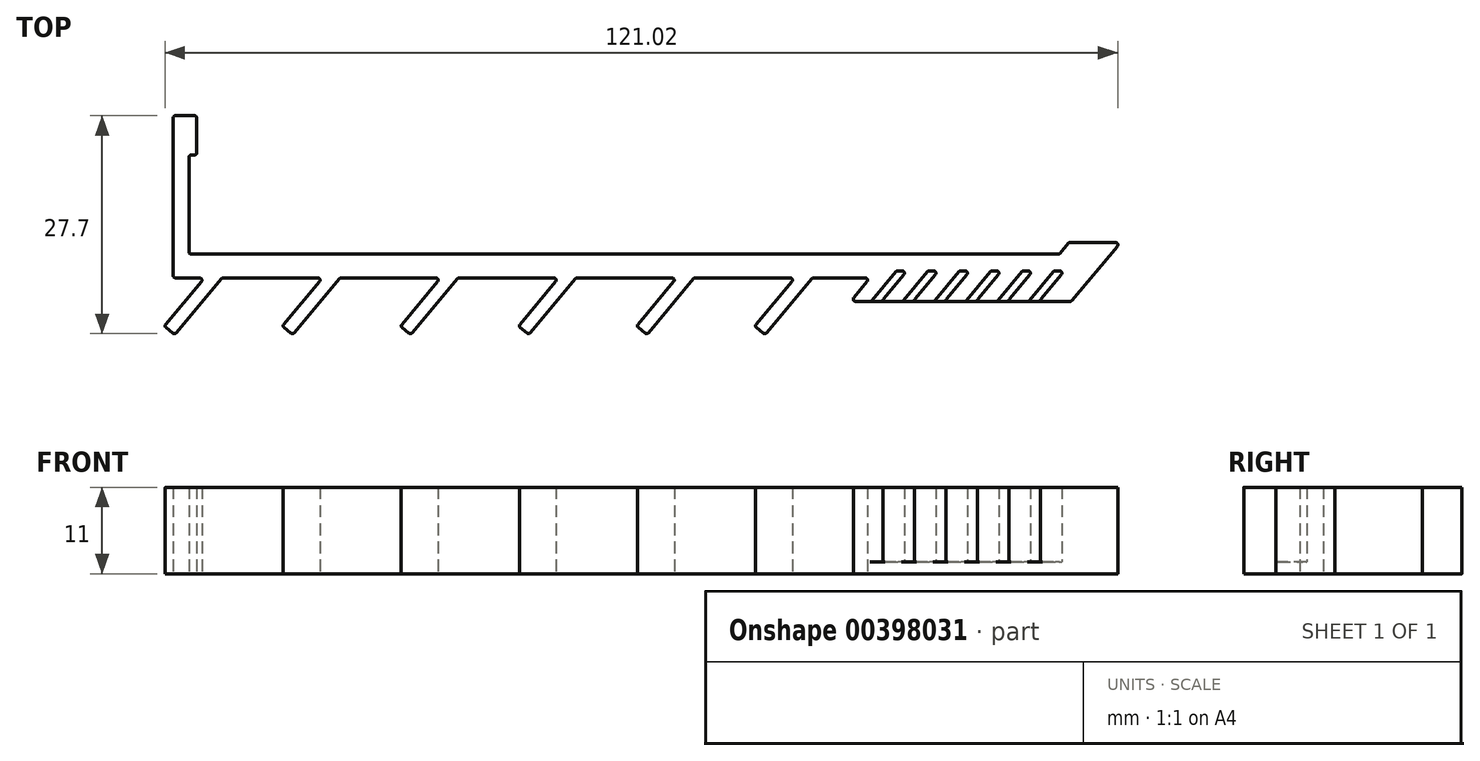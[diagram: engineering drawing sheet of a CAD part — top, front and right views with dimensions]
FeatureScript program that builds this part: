
annotation { "Feature Type Name" : "Feature", "Feature Type Description" : "" }
export const myFeature = defineFeature(function(context is Context, id is Id, definition is map)
    precondition{}
    {
        {
            var Q0;
            Q0=qCreatedBy(makeId("Top.planeOp"),FACE);
            var sketch = newSketch(context, id + "F0", { "sketchPlane" : qUnion([Q0])});
            skLineSegment(sketch, "E0", {"start": v(-67.4, 20.3) * mm, "end": v(-67.4, 0.3) * mm});
            skLineSegment(sketch, "E1", {"start": v(45.02, 3) * mm, "end": v(-65.1, 3) * mm});
            skLineSegment(sketch, "E2", {"start": v(-64.7, 20.6) * mm, "end": v(-67.1, 20.6) * mm});
            skLineSegment(sketch, "E3", {"start": v(-65.4, 3.3) * mm, "end": v(-65.4, 15.3) * mm});
            skLineSegment(sketch, "E4", {"start": v(-65.1, 15.6) * mm, "end": v(-64.7, 15.6) * mm});
            skLineSegment(sketch, "E5.trimOffspring", {"start": v(-64.4, 15.9) * mm, "end": v(-64.4, 20.3) * mm});
            skPoint(sketch, "E6.visualSharp", {"position": v(-64.4, 15.6) * mm});
            skArc(sketch, "E6.filletArc", {"start": v(-64.7, 15.6) * mm, "mid": v(-64.49, 15.69) * mm, "end": v(-64.4, 15.9) * mm});
            skPoint(sketch, "E7.visualSharp", {"position": v(-65.4, 15.6) * mm});
            skArc(sketch, "E7.filletArc", {"start": v(-65.1, 15.6) * mm, "mid": v(-65.31, 15.51) * mm, "end": v(-65.4, 15.3) * mm});
            skPoint(sketch, "E8.visualSharp", {"position": v(-64.4, 20.6) * mm});
            skArc(sketch, "E8.filletArc", {"start": v(-64.4, 20.3) * mm, "mid": v(-64.49, 20.51) * mm, "end": v(-64.7, 20.6) * mm});
            skPoint(sketch, "E9.visualSharp", {"position": v(-67.4, 20.6) * mm});
            skArc(sketch, "E9.filletArc", {"start": v(-67.1, 20.6) * mm, "mid": v(-67.31, 20.51) * mm, "end": v(-67.4, 20.3) * mm});
            skPoint(sketch, "E10.visualSharp", {"position": v(-67.4, 0) * mm});
            skArc(sketch, "E10.filletArc", {"start": v(-67.4, 0.3) * mm, "mid": v(-67.31, 0.09) * mm, "end": v(-67.1, 0) * mm});
            skLineSegment(sketch, "E11", {"start": v(-63.81, -0.5) * mm, "end": v(-68.35, -5.9) * mm});
            skLineSegment(sketch, "E12", {"start": v(-68.31, -6.32) * mm, "end": v(-67.47, -7.03) * mm});
            skLineSegment(sketch, "E13", {"start": v(-67.05, -7) * mm, "end": v(-61.27, -0.1) * mm});
            skLineSegment(sketch, "E14.1.0.0", {"start": v(-53.31, -6.32) * mm, "end": v(-52.47, -7.03) * mm});
            skLineSegment(sketch, "E14.1.0.1", {"start": v(-52.05, -7) * mm, "end": v(-46.27, -0.1) * mm});
            skLineSegment(sketch, "E14.1.0.2", {"start": v(-48.81, -0.5) * mm, "end": v(-53.35, -5.9) * mm});
            skLineSegment(sketch, "E14.2.0.0", {"start": v(-38.31, -6.32) * mm, "end": v(-37.47, -7.03) * mm});
            skLineSegment(sketch, "E14.2.0.1", {"start": v(-37.05, -7) * mm, "end": v(-31.27, -0.1) * mm});
            skLineSegment(sketch, "E14.2.0.2", {"start": v(-33.81, -0.5) * mm, "end": v(-38.35, -5.9) * mm});
            skLineSegment(sketch, "E14.3.0.0", {"start": v(-23.31, -6.32) * mm, "end": v(-22.47, -7.03) * mm});
            skLineSegment(sketch, "E14.3.0.1", {"start": v(-22.05, -7) * mm, "end": v(-16.27, -0.1) * mm});
            skLineSegment(sketch, "E14.3.0.2", {"start": v(-18.81, -0.5) * mm, "end": v(-23.35, -5.9) * mm});
            skLineSegment(sketch, "E14.4.0.0", {"start": v(-8.31, -6.32) * mm, "end": v(-7.47, -7.03) * mm});
            skLineSegment(sketch, "E14.4.0.1", {"start": v(-7.05, -7) * mm, "end": v(-1.27, -0.1) * mm});
            skLineSegment(sketch, "E14.4.0.2", {"start": v(-3.81, -0.5) * mm, "end": v(-8.35, -5.9) * mm});
            skLineSegment(sketch, "E14.5.0.0", {"start": v(6.69, -6.32) * mm, "end": v(7.53, -7.03) * mm});
            skLineSegment(sketch, "E14.5.0.1", {"start": v(7.95, -7) * mm, "end": v(13.73, -0.1) * mm});
            skLineSegment(sketch, "E14.5.0.2", {"start": v(11.19, -0.5) * mm, "end": v(6.65, -5.9) * mm});
            skLineSegment(sketch, "E14.direction1", {"start": v(-68.54, -6.13) * mm, "end": v(-53.54, -6.13) * mm, "construction": true});
            skLineSegment(sketch, "E15.top", {"start": v(19.3, -3) * mm, "end": v(21.12, -3) * mm});
            skLineSegment(sketch, "E15.left", {"start": v(20.75, -0.5) * mm, "end": v(19.06, -2.5) * mm});
            skLineSegment(sketch, "E16", {"start": v(20.52, 0) * mm, "end": v(13.96, 0) * mm});
            skLineSegment(sketch, "E17", {"start": v(10.96, 0) * mm, "end": v(-1.04, 0) * mm});
            skLineSegment(sketch, "E18", {"start": v(-4.04, 0) * mm, "end": v(-16.04, 0) * mm});
            skLineSegment(sketch, "E19", {"start": v(-19.04, 0) * mm, "end": v(-31.04, 0) * mm});
            skLineSegment(sketch, "E20", {"start": v(-34.04, 0) * mm, "end": v(-46.04, 0) * mm});
            skLineSegment(sketch, "E21", {"start": v(-49.04, 0) * mm, "end": v(-61.04, 0) * mm});
            skLineSegment(sketch, "E22", {"start": v(-64.04, 0) * mm, "end": v(-67.1, 0) * mm});
            skLineSegment(sketch, "E23", {"start": v(52.53, 4) * mm, "end": v(46.74, -2.9) * mm});
            skPoint(sketch, "E24.visualSharp", {"position": v(46.65, -3) * mm});
            skArc(sketch, "E24.filletArc", {"start": v(46.51, -3) * mm, "mid": v(46.64, -2.97) * mm, "end": v(46.74, -2.9) * mm});
            skPoint(sketch, "E25.visualSharp", {"position": v(18.65, -3) * mm});
            skArc(sketch, "E25.filletArc", {"start": v(19.06, -2.5) * mm, "mid": v(19.02, -2.83) * mm, "end": v(19.3, -3) * mm});
            skArc(sketch, "E26.filletArc", {"start": v(20.75, -0.5) * mm, "mid": v(20.8, -0.17) * mm, "end": v(20.52, 0) * mm});
            skPoint(sketch, "E27.visualSharp", {"position": v(-61.18, 0) * mm});
            skArc(sketch, "E27.filletArc", {"start": v(-61.04, 0) * mm, "mid": v(-61.17, -0.03) * mm, "end": v(-61.27, -0.1) * mm});
            skPoint(sketch, "E28.visualSharp", {"position": v(-63.4, 0) * mm});
            skArc(sketch, "E28.filletArc", {"start": v(-63.81, -0.5) * mm, "mid": v(-63.77, -0.17) * mm, "end": v(-64.04, 0) * mm});
            skPoint(sketch, "E29.visualSharp", {"position": v(-48.4, 0) * mm});
            skArc(sketch, "E29.filletArc", {"start": v(-48.81, -0.5) * mm, "mid": v(-48.77, -0.17) * mm, "end": v(-49.04, 0) * mm});
            skPoint(sketch, "E30.visualSharp", {"position": v(-46.18, 0) * mm});
            skArc(sketch, "E30.filletArc", {"start": v(-46.04, 0) * mm, "mid": v(-46.17, -0.03) * mm, "end": v(-46.27, -0.1) * mm});
            skPoint(sketch, "E31.visualSharp", {"position": v(-33.4, 0) * mm});
            skArc(sketch, "E31.filletArc", {"start": v(-33.81, -0.5) * mm, "mid": v(-33.77, -0.17) * mm, "end": v(-34.04, 0) * mm});
            skPoint(sketch, "E32.visualSharp", {"position": v(-31.18, 0) * mm});
            skArc(sketch, "E32.filletArc", {"start": v(-31.04, 0) * mm, "mid": v(-31.17, -0.03) * mm, "end": v(-31.27, -0.1) * mm});
            skPoint(sketch, "E33.visualSharp", {"position": v(-18.4, 0) * mm});
            skArc(sketch, "E33.filletArc", {"start": v(-18.81, -0.5) * mm, "mid": v(-18.77, -0.17) * mm, "end": v(-19.04, 0) * mm});
            skPoint(sketch, "E34.visualSharp", {"position": v(-16.18, 0) * mm});
            skArc(sketch, "E34.filletArc", {"start": v(-16.04, 0) * mm, "mid": v(-16.17, -0.03) * mm, "end": v(-16.27, -0.1) * mm});
            skPoint(sketch, "E35.visualSharp", {"position": v(-3.4, 0) * mm});
            skArc(sketch, "E35.filletArc", {"start": v(-3.81, -0.5) * mm, "mid": v(-3.77, -0.17) * mm, "end": v(-4.04, 0) * mm});
            skPoint(sketch, "E36.visualSharp", {"position": v(-1.18, 0) * mm});
            skArc(sketch, "E36.filletArc", {"start": v(-1.04, 0) * mm, "mid": v(-1.17, -0.03) * mm, "end": v(-1.27, -0.1) * mm});
            skPoint(sketch, "E37.visualSharp", {"position": v(11.6, 0) * mm});
            skArc(sketch, "E37.filletArc", {"start": v(11.19, -0.5) * mm, "mid": v(11.23, -0.17) * mm, "end": v(10.96, 0) * mm});
            skPoint(sketch, "E38.visualSharp", {"position": v(13.82, 0) * mm});
            skArc(sketch, "E38.filletArc", {"start": v(13.96, 0) * mm, "mid": v(13.83, -0.03) * mm, "end": v(13.73, -0.1) * mm});
            skPoint(sketch, "E39.visualSharp", {"position": v(7.76, -7.22) * mm});
            skArc(sketch, "E39.filletArc", {"start": v(7.53, -7.03) * mm, "mid": v(7.75, -7.1) * mm, "end": v(7.95, -7) * mm});
            skPoint(sketch, "E40.visualSharp", {"position": v(6.46, -6.13) * mm});
            skArc(sketch, "E40.filletArc", {"start": v(6.65, -5.9) * mm, "mid": v(6.58, -6.12) * mm, "end": v(6.69, -6.32) * mm});
            skPoint(sketch, "E41.visualSharp", {"position": v(-7.24, -7.22) * mm});
            skArc(sketch, "E41.filletArc", {"start": v(-7.47, -7.03) * mm, "mid": v(-7.25, -7.1) * mm, "end": v(-7.05, -7) * mm});
            skPoint(sketch, "E42.visualSharp", {"position": v(-8.54, -6.13) * mm});
            skArc(sketch, "E42.filletArc", {"start": v(-8.35, -5.9) * mm, "mid": v(-8.42, -6.12) * mm, "end": v(-8.31, -6.32) * mm});
            skPoint(sketch, "E43.visualSharp", {"position": v(-23.54, -6.13) * mm});
            skArc(sketch, "E43.filletArc", {"start": v(-23.35, -5.9) * mm, "mid": v(-23.42, -6.12) * mm, "end": v(-23.31, -6.32) * mm});
            skPoint(sketch, "E44.visualSharp", {"position": v(-22.24, -7.22) * mm});
            skArc(sketch, "E44.filletArc", {"start": v(-22.47, -7.03) * mm, "mid": v(-22.25, -7.1) * mm, "end": v(-22.05, -7) * mm});
            skPoint(sketch, "E45.visualSharp", {"position": v(-53.54, -6.13) * mm});
            skArc(sketch, "E45.filletArc", {"start": v(-53.35, -5.9) * mm, "mid": v(-53.42, -6.12) * mm, "end": v(-53.31, -6.32) * mm});
            skPoint(sketch, "E46.visualSharp", {"position": v(-52.24, -7.22) * mm});
            skArc(sketch, "E46.filletArc", {"start": v(-52.47, -7.03) * mm, "mid": v(-52.25, -7.1) * mm, "end": v(-52.05, -7) * mm});
            skPoint(sketch, "E47.visualSharp", {"position": v(-38.54, -6.13) * mm});
            skArc(sketch, "E47.filletArc", {"start": v(-38.35, -5.9) * mm, "mid": v(-38.42, -6.12) * mm, "end": v(-38.31, -6.32) * mm});
            skPoint(sketch, "E48.visualSharp", {"position": v(-37.24, -7.22) * mm});
            skArc(sketch, "E48.filletArc", {"start": v(-37.47, -7.03) * mm, "mid": v(-37.25, -7.1) * mm, "end": v(-37.05, -7) * mm});
            skPoint(sketch, "E49.visualSharp", {"position": v(-67.24, -7.22) * mm});
            skArc(sketch, "E49.filletArc", {"start": v(-67.47, -7.03) * mm, "mid": v(-67.25, -7.1) * mm, "end": v(-67.05, -7) * mm});
            skPoint(sketch, "E50.visualSharp", {"position": v(-68.54, -6.13) * mm});
            skArc(sketch, "E50.filletArc", {"start": v(-68.35, -5.9) * mm, "mid": v(-68.42, -6.12) * mm, "end": v(-68.31, -6.32) * mm});
            skLineSegment(sketch, "E51", {"start": v(21.35, -2.9) * mm, "end": v(24.44, 0.78) * mm});
            skLineSegment(sketch, "E52", {"start": v(24.67, 0.9) * mm, "end": v(25.19, 0.9) * mm});
            skLineSegment(sketch, "E53", {"start": v(25.42, 0.4) * mm, "end": v(22.84, -2.67) * mm});
            skArc(sketch, "E54.filletArc", {"start": v(21.12, -3) * mm, "mid": v(21.25, -2.97) * mm, "end": v(21.35, -2.9) * mm});
            skLineSegment(sketch, "E55", {"start": v(27, -3) * mm, "end": v(29.12, -3) * mm});
            skArc(sketch, "E56.filletArc", {"start": v(22.84, -2.67) * mm, "mid": v(22.81, -2.88) * mm, "end": v(23, -3) * mm});
            skArc(sketch, "E57.filletArc", {"start": v(25.42, 0.4) * mm, "mid": v(25.46, 0.72) * mm, "end": v(25.19, 0.9) * mm});
            skPoint(sketch, "E58.visualSharp", {"position": v(24.53, 0.9) * mm});
            skArc(sketch, "E58.filletArc", {"start": v(24.67, 0.9) * mm, "mid": v(24.54, 0.86) * mm, "end": v(24.44, 0.78) * mm});
            skArc(sketch, "E59.1.0.0", {"start": v(29.42, 0.4) * mm, "mid": v(29.46, 0.72) * mm, "end": v(29.19, 0.9) * mm});
            skPoint(sketch, "E59.1.0.1", {"position": v(28.53, 0.9) * mm});
            skArc(sketch, "E59.1.0.2", {"start": v(26.84, -2.67) * mm, "mid": v(26.81, -2.88) * mm, "end": v(27, -3) * mm});
            skLineSegment(sketch, "E59.1.0.3", {"start": v(29.42, 0.4) * mm, "end": v(26.84, -2.67) * mm});
            skLineSegment(sketch, "E59.1.0.5", {"start": v(25.35, -2.9) * mm, "end": v(28.44, 0.78) * mm});
            skLineSegment(sketch, "E59.1.0.6", {"start": v(28.67, 0.9) * mm, "end": v(29.19, 0.9) * mm});
            skArc(sketch, "E59.1.0.7", {"start": v(28.67, 0.9) * mm, "mid": v(28.54, 0.86) * mm, "end": v(28.44, 0.78) * mm});
            skArc(sketch, "E59.1.0.8", {"start": v(25.12, -3) * mm, "mid": v(25.25, -2.97) * mm, "end": v(25.35, -2.9) * mm});
            skArc(sketch, "E59.2.0.0", {"start": v(33.42, 0.4) * mm, "mid": v(33.46, 0.72) * mm, "end": v(33.19, 0.9) * mm});
            skPoint(sketch, "E59.2.0.1", {"position": v(32.53, 0.9) * mm});
            skArc(sketch, "E59.2.0.2", {"start": v(30.84, -2.67) * mm, "mid": v(30.81, -2.88) * mm, "end": v(31, -3) * mm});
            skLineSegment(sketch, "E59.2.0.3", {"start": v(33.42, 0.4) * mm, "end": v(30.84, -2.67) * mm});
            skLineSegment(sketch, "E59.2.0.5", {"start": v(29.35, -2.9) * mm, "end": v(32.44, 0.78) * mm});
            skLineSegment(sketch, "E59.2.0.6", {"start": v(32.67, 0.9) * mm, "end": v(33.19, 0.9) * mm});
            skArc(sketch, "E59.2.0.7", {"start": v(32.67, 0.9) * mm, "mid": v(32.54, 0.86) * mm, "end": v(32.44, 0.78) * mm});
            skArc(sketch, "E59.2.0.8", {"start": v(29.12, -3) * mm, "mid": v(29.25, -2.97) * mm, "end": v(29.35, -2.9) * mm});
            skArc(sketch, "E59.3.0.0", {"start": v(37.42, 0.4) * mm, "mid": v(37.46, 0.72) * mm, "end": v(37.19, 0.9) * mm});
            skPoint(sketch, "E59.3.0.1", {"position": v(36.53, 0.9) * mm});
            skArc(sketch, "E59.3.0.2", {"start": v(34.84, -2.67) * mm, "mid": v(34.81, -2.88) * mm, "end": v(35, -3) * mm});
            skLineSegment(sketch, "E59.3.0.3", {"start": v(37.42, 0.4) * mm, "end": v(34.84, -2.67) * mm});
            skLineSegment(sketch, "E59.3.0.5", {"start": v(33.35, -2.9) * mm, "end": v(36.44, 0.78) * mm});
            skLineSegment(sketch, "E59.3.0.6", {"start": v(36.67, 0.9) * mm, "end": v(37.19, 0.9) * mm});
            skArc(sketch, "E59.3.0.7", {"start": v(36.67, 0.9) * mm, "mid": v(36.54, 0.86) * mm, "end": v(36.44, 0.78) * mm});
            skArc(sketch, "E59.3.0.8", {"start": v(33.12, -3) * mm, "mid": v(33.25, -2.97) * mm, "end": v(33.35, -2.9) * mm});
            skArc(sketch, "E59.4.0.0", {"start": v(41.42, 0.4) * mm, "mid": v(41.46, 0.72) * mm, "end": v(41.19, 0.9) * mm});
            skPoint(sketch, "E59.4.0.1", {"position": v(40.53, 0.9) * mm});
            skArc(sketch, "E59.4.0.2", {"start": v(38.84, -2.67) * mm, "mid": v(38.81, -2.88) * mm, "end": v(39, -3) * mm});
            skLineSegment(sketch, "E59.4.0.3", {"start": v(41.42, 0.4) * mm, "end": v(38.84, -2.67) * mm});
            skLineSegment(sketch, "E59.4.0.5", {"start": v(37.35, -2.9) * mm, "end": v(40.44, 0.78) * mm});
            skLineSegment(sketch, "E59.4.0.6", {"start": v(40.67, 0.9) * mm, "end": v(41.19, 0.9) * mm});
            skArc(sketch, "E59.4.0.7", {"start": v(40.67, 0.9) * mm, "mid": v(40.54, 0.86) * mm, "end": v(40.44, 0.78) * mm});
            skArc(sketch, "E59.4.0.8", {"start": v(37.12, -3) * mm, "mid": v(37.25, -2.97) * mm, "end": v(37.35, -2.9) * mm});
            skArc(sketch, "E59.5.0.0", {"start": v(45.42, 0.4) * mm, "mid": v(45.46, 0.72) * mm, "end": v(45.19, 0.9) * mm});
            skPoint(sketch, "E59.5.0.1", {"position": v(44.53, 0.9) * mm});
            skArc(sketch, "E59.5.0.2", {"start": v(42.84, -2.67) * mm, "mid": v(42.81, -2.88) * mm, "end": v(43, -3) * mm});
            skLineSegment(sketch, "E59.5.0.3", {"start": v(45.42, 0.4) * mm, "end": v(42.84, -2.67) * mm});
            skLineSegment(sketch, "E59.5.0.5", {"start": v(41.35, -2.9) * mm, "end": v(44.44, 0.78) * mm});
            skLineSegment(sketch, "E59.5.0.6", {"start": v(44.67, 0.9) * mm, "end": v(45.19, 0.9) * mm});
            skArc(sketch, "E59.5.0.7", {"start": v(44.67, 0.9) * mm, "mid": v(44.54, 0.86) * mm, "end": v(44.44, 0.78) * mm});
            skArc(sketch, "E59.5.0.8", {"start": v(41.12, -3) * mm, "mid": v(41.25, -2.97) * mm, "end": v(41.35, -2.9) * mm});
            skLineSegment(sketch, "E59.direction1", {"start": v(21.12, -3) * mm, "end": v(25.12, -3) * mm, "construction": true});
            skLineSegment(sketch, "E60.trimOffspring", {"start": v(31, -3) * mm, "end": v(33.12, -3) * mm});
            skLineSegment(sketch, "E61.trimOffspring", {"start": v(35, -3) * mm, "end": v(37.12, -3) * mm});
            skLineSegment(sketch, "E62.trimOffspring", {"start": v(39, -3) * mm, "end": v(41.12, -3) * mm});
            skLineSegment(sketch, "E63.trimOffspring", {"start": v(43, -3) * mm, "end": v(46.51, -3) * mm});
            skLineSegment(sketch, "E64", {"start": v(23, -3) * mm, "end": v(25.12, -3) * mm});
            skPoint(sketch, "E65.visualSharp", {"position": v(-65.4, 3) * mm});
            skArc(sketch, "E65.filletArc", {"start": v(-65.4, 3.3) * mm, "mid": v(-65.31, 3.09) * mm, "end": v(-65.1, 3) * mm});
            skLineSegment(sketch, "E66", {"start": v(52.3, 4.5) * mm, "end": v(46.56, 4.5) * mm});
            skLineSegment(sketch, "E67", {"start": v(46.33, 4.4) * mm, "end": v(45.25, 3.1) * mm});
            skArc(sketch, "E68.filletArc", {"start": v(52.53, 4) * mm, "mid": v(52.57, 4.33) * mm, "end": v(52.3, 4.5) * mm});
            skArc(sketch, "E69.filletArc", {"start": v(46.56, 4.5) * mm, "mid": v(46.43, 4.47) * mm, "end": v(46.33, 4.4) * mm});
            skPoint(sketch, "E70.visualSharp", {"position": v(45.16, 3) * mm});
            skArc(sketch, "E70.filletArc", {"start": v(45.02, 3) * mm, "mid": v(45.14, 3.03) * mm, "end": v(45.25, 3.1) * mm});
            skSolve(sketch);
        }
        {
            var Q0;
            Q0=makeQuery(id+"F0.imprint","IMPRINT",FACE,{"disambiguationData":[TD([[makeQuery(id+"F0.imprint","IMPRINT",EDGE,{"derivedFrom":sQuery(id+"F0.wireOp",EDGE,"E0")}),1.0]])]});
            extrude(context, id + "F1", {"entities" : qUnion([Q0]), "depth" : 11 * mm});
        }
        {
            var Q0;
            Q0=makeQuery(id+"F1.opExtrude","CAP_FACE",FACE,{"disambiguationData":[OSD([sQuery(id+"F0.wireOp",EDGE,"E0"),sQuery(id+"F0.wireOp",EDGE,"E1"),sQuery(id+"F0.wireOp",EDGE,"cCio9jsE-9EY3-OPMo-t5Gu-vrGkitFTGGda"),sQuery(id+"F0.wireOp",EDGE,"E2"),sQuery(id+"F0.wireOp",EDGE,"H533jxHk-3XtM-Z6vW-Bzfs-BtqaTveMGdZc"),sQuery(id+"F0.wireOp",EDGE,"E3"),sQuery(id+"F0.wireOp",EDGE,"E4"),sQuery(id+"F0.wireOp",EDGE,"E5.trimOffspring"),sQuery(id+"F0.wireOp",EDGE,"E6.filletArc"),sQuery(id+"F0.wireOp",EDGE,"E7.filletArc"),sQuery(id+"F0.wireOp",EDGE,"dc431e2b-7f99-421d-aafe-299582165b38.filletArc"),sQuery(id+"F0.wireOp",EDGE,"12db450a-c5aa-48bc-ba82-543e06b74559.filletArc"),sQuery(id+"F0.wireOp",EDGE,"ebcc2041-b316-4c20-95a7-d6591fa13ea7.filletArc"),sQuery(id+"F0.wireOp",EDGE,"E8.filletArc"),sQuery(id+"F0.wireOp",EDGE,"E9.filletArc"),sQuery(id+"F0.wireOp",EDGE,"E10.filletArc"),sQuery(id+"F0.wireOp",EDGE,"de8ec55a-9d5e-4987-a20f-71df37a005a4.filletArc"),sQuery(id+"F0.wireOp",EDGE,"E11"),sQuery(id+"F0.wireOp",EDGE,"E12"),sQuery(id+"F0.wireOp",EDGE,"E13"),sQuery(id+"F0.wireOp",EDGE,"E14.1.0.0"),sQuery(id+"F0.wireOp",EDGE,"E14.1.0.1"),sQuery(id+"F0.wireOp",EDGE,"E14.1.0.2"),sQuery(id+"F0.wireOp",EDGE,"E14.2.0.0"),sQuery(id+"F0.wireOp",EDGE,"E14.2.0.1"),sQuery(id+"F0.wireOp",EDGE,"E14.2.0.2"),sQuery(id+"F0.wireOp",EDGE,"E14.3.0.0"),sQuery(id+"F0.wireOp",EDGE,"E14.3.0.1"),sQuery(id+"F0.wireOp",EDGE,"E14.3.0.2"),sQuery(id+"F0.wireOp",EDGE,"E14.4.0.0"),sQuery(id+"F0.wireOp",EDGE,"E14.4.0.1"),sQuery(id+"F0.wireOp",EDGE,"E14.4.0.2"),sQuery(id+"F0.wireOp",EDGE,"E14.5.0.0"),sQuery(id+"F0.wireOp",EDGE,"E14.5.0.1"),sQuery(id+"F0.wireOp",EDGE,"E14.5.0.2"),sQuery(id+"F0.wireOp",EDGE,"E15.top"),sQuery(id+"F0.wireOp",EDGE,"E15.left"),sQuery(id+"F0.wireOp",EDGE,"E16"),sQuery(id+"F0.wireOp",EDGE,"E17"),sQuery(id+"F0.wireOp",EDGE,"E18"),sQuery(id+"F0.wireOp",EDGE,"E19"),sQuery(id+"F0.wireOp",EDGE,"E20"),sQuery(id+"F0.wireOp",EDGE,"E21"),sQuery(id+"F0.wireOp",EDGE,"E22"),sQuery(id+"F0.wireOp",EDGE,"E23"),sQuery(id+"F0.wireOp",EDGE,"E24.filletArc"),sQuery(id+"F0.wireOp",EDGE,"E25.filletArc"),sQuery(id+"F0.wireOp",EDGE,"E26.filletArc"),sQuery(id+"F0.wireOp",EDGE,"E27.filletArc"),sQuery(id+"F0.wireOp",EDGE,"E28.filletArc"),sQuery(id+"F0.wireOp",EDGE,"E29.filletArc"),sQuery(id+"F0.wireOp",EDGE,"E30.filletArc"),sQuery(id+"F0.wireOp",EDGE,"E31.filletArc"),sQuery(id+"F0.wireOp",EDGE,"E32.filletArc"),sQuery(id+"F0.wireOp",EDGE,"E33.filletArc"),sQuery(id+"F0.wireOp",EDGE,"E34.filletArc"),sQuery(id+"F0.wireOp",EDGE,"E35.filletArc"),sQuery(id+"F0.wireOp",EDGE,"E36.filletArc"),sQuery(id+"F0.wireOp",EDGE,"E37.filletArc"),sQuery(id+"F0.wireOp",EDGE,"E38.filletArc"),sQuery(id+"F0.wireOp",EDGE,"E39.filletArc"),sQuery(id+"F0.wireOp",EDGE,"E40.filletArc"),sQuery(id+"F0.wireOp",EDGE,"E41.filletArc"),sQuery(id+"F0.wireOp",EDGE,"E42.filletArc"),sQuery(id+"F0.wireOp",EDGE,"E43.filletArc"),sQuery(id+"F0.wireOp",EDGE,"E44.filletArc"),sQuery(id+"F0.wireOp",EDGE,"E45.filletArc"),sQuery(id+"F0.wireOp",EDGE,"E46.filletArc"),sQuery(id+"F0.wireOp",EDGE,"E47.filletArc"),sQuery(id+"F0.wireOp",EDGE,"E48.filletArc"),sQuery(id+"F0.wireOp",EDGE,"E49.filletArc"),sQuery(id+"F0.wireOp",EDGE,"E50.filletArc"),sQuery(id+"F0.wireOp",EDGE,"E51"),sQuery(id+"F0.wireOp",EDGE,"E52"),sQuery(id+"F0.wireOp",EDGE,"E53"),sQuery(id+"F0.wireOp",EDGE,"E54.filletArc"),sQuery(id+"F0.wireOp",EDGE,"E55"),sQuery(id+"F0.wireOp",EDGE,"E56.filletArc"),sQuery(id+"F0.wireOp",EDGE,"E57.filletArc"),sQuery(id+"F0.wireOp",EDGE,"E58.filletArc"),sQuery(id+"F0.wireOp",EDGE,"E59.1.0.0"),sQuery(id+"F0.wireOp",EDGE,"E59.1.0.2"),sQuery(id+"F0.wireOp",EDGE,"E59.1.0.3"),sQuery(id+"F0.wireOp",EDGE,"E59.1.0.5"),sQuery(id+"F0.wireOp",EDGE,"E59.1.0.6"),sQuery(id+"F0.wireOp",EDGE,"E59.1.0.7"),sQuery(id+"F0.wireOp",EDGE,"E59.1.0.8"),sQuery(id+"F0.wireOp",EDGE,"E59.2.0.0"),sQuery(id+"F0.wireOp",EDGE,"E59.2.0.2"),sQuery(id+"F0.wireOp",EDGE,"E59.2.0.3"),sQuery(id+"F0.wireOp",EDGE,"E59.2.0.5"),sQuery(id+"F0.wireOp",EDGE,"E59.2.0.6"),sQuery(id+"F0.wireOp",EDGE,"E59.2.0.7"),sQuery(id+"F0.wireOp",EDGE,"E59.2.0.8"),sQuery(id+"F0.wireOp",EDGE,"E59.3.0.0"),sQuery(id+"F0.wireOp",EDGE,"E59.3.0.2"),sQuery(id+"F0.wireOp",EDGE,"E59.3.0.3"),sQuery(id+"F0.wireOp",EDGE,"E59.3.0.5"),sQuery(id+"F0.wireOp",EDGE,"E59.3.0.6"),sQuery(id+"F0.wireOp",EDGE,"E59.3.0.7"),sQuery(id+"F0.wireOp",EDGE,"E59.3.0.8"),sQuery(id+"F0.wireOp",EDGE,"E59.4.0.0"),sQuery(id+"F0.wireOp",EDGE,"E59.4.0.2"),sQuery(id+"F0.wireOp",EDGE,"E59.4.0.3"),sQuery(id+"F0.wireOp",EDGE,"E59.4.0.5"),sQuery(id+"F0.wireOp",EDGE,"E59.4.0.6"),sQuery(id+"F0.wireOp",EDGE,"E59.4.0.7"),sQuery(id+"F0.wireOp",EDGE,"E59.4.0.8"),sQuery(id+"F0.wireOp",EDGE,"E59.5.0.0"),sQuery(id+"F0.wireOp",EDGE,"E59.5.0.2"),sQuery(id+"F0.wireOp",EDGE,"E59.5.0.3"),sQuery(id+"F0.wireOp",EDGE,"E59.5.0.5"),sQuery(id+"F0.wireOp",EDGE,"E59.5.0.6"),sQuery(id+"F0.wireOp",EDGE,"E59.5.0.7"),sQuery(id+"F0.wireOp",EDGE,"E59.5.0.8"),sQuery(id+"F0.wireOp",EDGE,"E60.trimOffspring"),sQuery(id+"F0.wireOp",EDGE,"E61.trimOffspring"),sQuery(id+"F0.wireOp",EDGE,"E62.trimOffspring"),sQuery(id+"F0.wireOp",EDGE,"E63.trimOffspring"),sQuery(id+"F0.wireOp",EDGE,"E64")])],"isStart":true});
            var sketch = newSketch(context, id + "F2", { "sketchPlane" : qUnion([Q0])});
            skLineSegment(sketch, "E71", {"start": v(51.04, -3) * mm, "end": v(23.68, -3) * mm});
            skLineSegment(sketch, "E72", {"start": v(23.68, -3) * mm, "end": v(19.06, 2.5) * mm});
            skLineSegment(sketch, "E73", {"start": v(19.3, 3) * mm, "end": v(46.51, 3) * mm});
            skLineSegment(sketch, "E74", {"start": v(46.74, 2.9) * mm, "end": v(51.27, -2.5) * mm});
            skPoint(sketch, "E75.visualSharp", {"position": v(51.68, -3) * mm});
            skArc(sketch, "E75.filletArc", {"start": v(51.04, -3) * mm, "mid": v(51.31, -2.83) * mm, "end": v(51.27, -2.5) * mm});
            skPoint(sketch, "E76.visualSharp", {"position": v(46.65, 3) * mm});
            skArc(sketch, "E76.filletArc", {"start": v(46.74, 2.9) * mm, "mid": v(46.64, 2.97) * mm, "end": v(46.51, 3) * mm});
            skPoint(sketch, "E77.visualSharp", {"position": v(18.65, 3) * mm});
            skArc(sketch, "E77.filletArc", {"start": v(19.3, 3) * mm, "mid": v(19.02, 2.83) * mm, "end": v(19.06, 2.5) * mm});
            skSolve(sketch);
        }
        {
            var Q0;
            Q0 = qSketchRegion(id + "F2", true);
            extrude(context, id + "F3", {"entities" : qUnion([Q0]), "operationType" : NewBodyOperationType.ADD, "oppositeDirection" : true, "depth" : 1.5 * mm});
        }
    });
